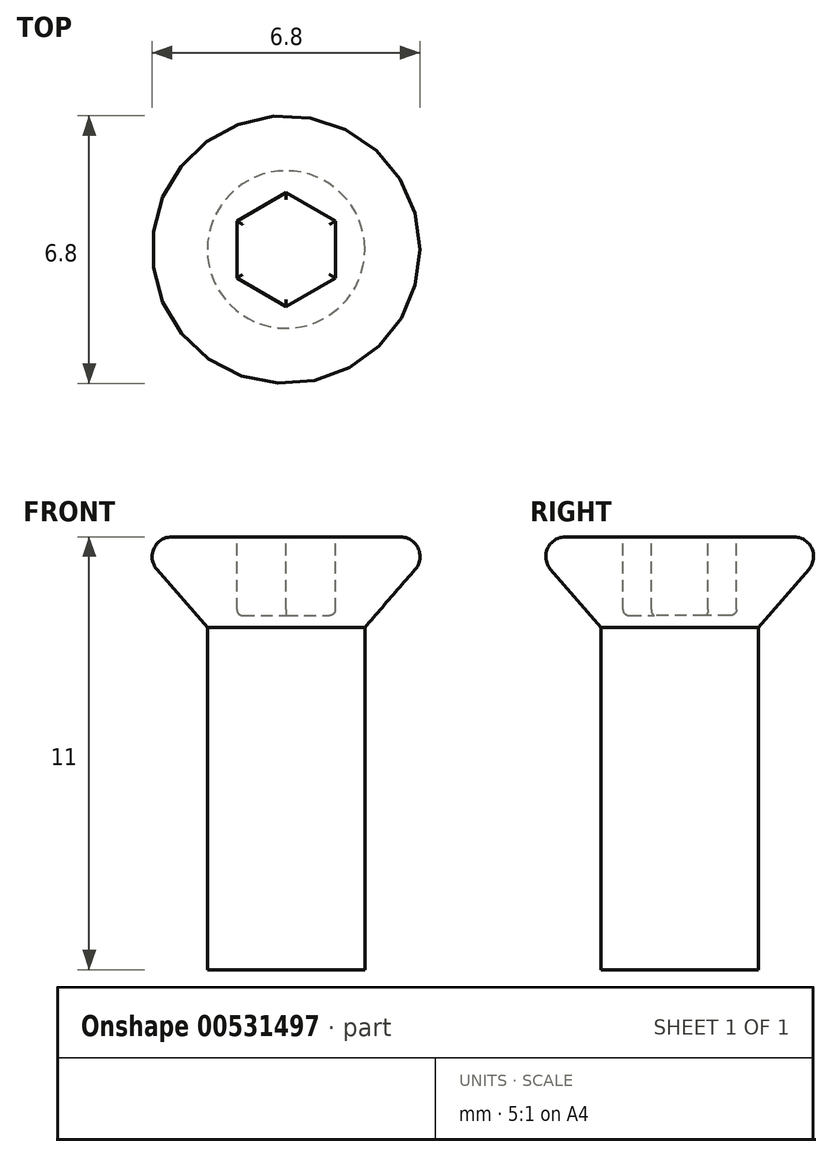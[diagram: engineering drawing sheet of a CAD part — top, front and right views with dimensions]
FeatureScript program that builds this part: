
annotation { "Feature Type Name" : "Feature", "Feature Type Description" : "" }
export const myFeature = defineFeature(function(context is Context, id is Id, definition is map)
    precondition{}
    {
        {
            var Q0;
            Q0=qCreatedBy(makeId("Top.planeOp"),FACE);
            var sketch = newSketch(context, id + "F0", { "sketchPlane" : qUnion([Q0])});
            skCircle(sketch, "E0", {"center": v(0, 0) * mm, "radius": 4 * mm});
            skSolve(sketch);
        }
        {
            var Q0;
            Q0=qCreatedBy(makeId("Top.planeOp"),FACE);
            cPlane(context, id + "F1", {"entities" : qUnion([Q0]), "cplaneType" : CPlaneType.OFFSET, "offset" : 2.3 * mm, "oppositeDirection" : true, "width" : 150 * mm, "height" : 150 * mm});
        }
        {
            var Q0;
            Q0=qCreatedBy(id+"F1.planeOp",FACE);
            var sketch = newSketch(context, id + "F2", { "sketchPlane" : qUnion([Q0])});
            skCircle(sketch, "E1", {"center": v(0, 0) * mm, "radius": 2 * mm});
            skSolve(sketch);
        }
        {
            var Q0;
            Q0=makeQuery(id+"F0.imprint","IMPRINT",FACE,{"disambiguationData":[TD([[makeQuery(id+"F0.imprint","IMPRINT",EDGE,{"derivedFrom":sQuery(id+"F0.wireOp",EDGE,"E0")}),1.0]])]});
            var Q1;
            Q1=makeQuery(id+"F2.imprint","IMPRINT",FACE,{"disambiguationData":[TD([[makeQuery(id+"F2.imprint","IMPRINT",EDGE,{"derivedFrom":sQuery(id+"F2.wireOp",EDGE,"E1")}),1.0]])]});
            loft(context, id + "F3", {"sheetProfilesArray" : [{ "sheetProfileEntities" : qUnion([Q0]) }, { "sheetProfileEntities" : qUnion([Q1]) }]});
        }
        {
            var Q0;
            Q0=makeQuery(id+"F3.opLoft","CAP_FACE",FACE,{"disambiguationData":[OSD([makeQuery(id+"F2.imprint","IMPRINT",FACE,{"disambiguationData":[TD([[makeQuery(id+"F2.imprint","IMPRINT",EDGE,{"derivedFrom":sQuery(id+"F2.wireOp",EDGE,"E1")}),1.0]])]})])],"isStart":true});
            extrude(context, id + "F4", {"entities" : qUnion([Q0]), "operationType" : NewBodyOperationType.ADD, "depth" : 8.7 * mm, "offsetDistance" : 25 * mm});
        }
        {
            var Q0;
            Q0=makeQuery(id+"F3.opLoft","CAP_FACE",FACE,{"disambiguationData":[OSD([makeQuery(id+"F0.imprint","IMPRINT",FACE,{"disambiguationData":[TD([[makeQuery(id+"F0.imprint","IMPRINT",EDGE,{"derivedFrom":sQuery(id+"F0.wireOp",EDGE,"E0")}),1.0]])]})])],"isStart":true});
            var sketch = newSketch(context, id + "F5", { "sketchPlane" : qUnion([Q0])});
            skCircle(sketch, "E2.cCircle", {"center": v(0, 0) * mm, "radius": 1.25 * mm, "construction": true});
            skLineSegment(sketch, "E2.0", {"start": v(1.25, 0.72) * mm, "end": v(1.25, -0.72) * mm});
            skLineSegment(sketch, "E2.1", {"start": v(1.25, -0.72) * mm, "end": v(0, -1.44) * mm});
            skLineSegment(sketch, "E2.2", {"start": v(0, -1.44) * mm, "end": v(-1.25, -0.72) * mm});
            skLineSegment(sketch, "E2.3", {"start": v(-1.25, -0.72) * mm, "end": v(-1.25, 0.72) * mm});
            skLineSegment(sketch, "E2.4", {"start": v(-1.25, 0.72) * mm, "end": v(0, 1.44) * mm});
            skLineSegment(sketch, "E2.5", {"start": v(0, 1.44) * mm, "end": v(1.25, 0.72) * mm});
            skPoint(sketch, "E2.0.midPoint", {"position": v(1.25, 0) * mm});
            skSolve(sketch);
        }
        {
            var Q0;
            Q0=makeQuery(id+"F5.imprint","IMPRINT",FACE,{"disambiguationData":[TD([[makeQuery(id+"F5.imprint","IMPRINT",EDGE,{"derivedFrom":sQuery(id+"F5.wireOp",EDGE,"E2.0")}),-1.0]])]});
            extrude(context, id + "F6", {"entities" : qUnion([Q0]), "operationType" : NewBodyOperationType.REMOVE, "oppositeDirection" : true, "depth" : 2 * mm, "offsetDistance" : 25 * mm});
        }
        {
            var Q0;
            Q0=makeQuery(id+"F6.boolean.opBoolean","COPY",FACE,{"derivedFrom":makeQuery(id+"F6.opExtrude","CAP_FACE",FACE,{"disambiguationData":[OSD([sQuery(id+"F5.wireOp",EDGE,"E2.0"),sQuery(id+"F5.wireOp",EDGE,"E2.1"),sQuery(id+"F5.wireOp",EDGE,"E2.2"),sQuery(id+"F5.wireOp",EDGE,"E2.3"),sQuery(id+"F5.wireOp",EDGE,"E2.4"),sQuery(id+"F5.wireOp",EDGE,"E2.5")])],"isStart":false})});
            var Q1;
            Q1=makeQuery(id+"F6.boolean.opBoolean","COPY",EDGE,{"derivedFrom":makeQuery(id+"F6.opExtrude","CAP_EDGE",EDGE,{"disambiguationData":[OSD([sQuery(id+"F5.wireOp",EDGE,"E2.4")])],"isStart":true})});
            var Q2;
            Q2=makeQuery(id+"F6.boolean.opBoolean","COPY",EDGE,{"derivedFrom":makeQuery(id+"F6.opExtrude","CAP_EDGE",EDGE,{"disambiguationData":[OSD([sQuery(id+"F5.wireOp",EDGE,"E2.5")])],"isStart":true})});
            var Q3;
            Q3=makeQuery(id+"F6.boolean.opBoolean","COPY",EDGE,{"derivedFrom":makeQuery(id+"F6.opExtrude","CAP_EDGE",EDGE,{"disambiguationData":[OSD([sQuery(id+"F5.wireOp",EDGE,"E2.0")])],"isStart":true})});
            var Q4;
            Q4=makeQuery(id+"F6.boolean.opBoolean","COPY",EDGE,{"derivedFrom":makeQuery(id+"F6.opExtrude","CAP_EDGE",EDGE,{"disambiguationData":[OSD([sQuery(id+"F5.wireOp",EDGE,"E2.1")])],"isStart":true})});
            var Q5;
            Q5=makeQuery(id+"F6.boolean.opBoolean","COPY",EDGE,{"derivedFrom":makeQuery(id+"F6.opExtrude","CAP_EDGE",EDGE,{"disambiguationData":[OSD([sQuery(id+"F5.wireOp",EDGE,"E2.2")])],"isStart":true})});
            var Q6;
            Q6=makeQuery(id+"F6.boolean.opBoolean","COPY",EDGE,{"derivedFrom":makeQuery(id+"F6.opExtrude","CAP_EDGE",EDGE,{"disambiguationData":[OSD([sQuery(id+"F5.wireOp",EDGE,"E2.3")])],"isStart":true})});
            fillet(context, id + "F7", {"entities" : qUnion([Q0, Q1, Q2, Q3, Q4, Q5, Q6]), "radius" : .15 * mm, "tangentPropagation" : true, "allowEdgeOverflow" : false});
        }
        {
            var Q0;
            Q0=makeQuery(id+"F3.opLoft","MID_CAP_EDGE",EDGE,{"disambiguationData":[OSD([sQuery(id+"F0.wireOp",EDGE,"E0")])],"capPos":0.0});
            fillet(context, id + "F8", {"entities" : qUnion([Q0]), "radius" : .5 * mm, "tangentPropagation" : true, "allowEdgeOverflow" : false});
        }
    });
